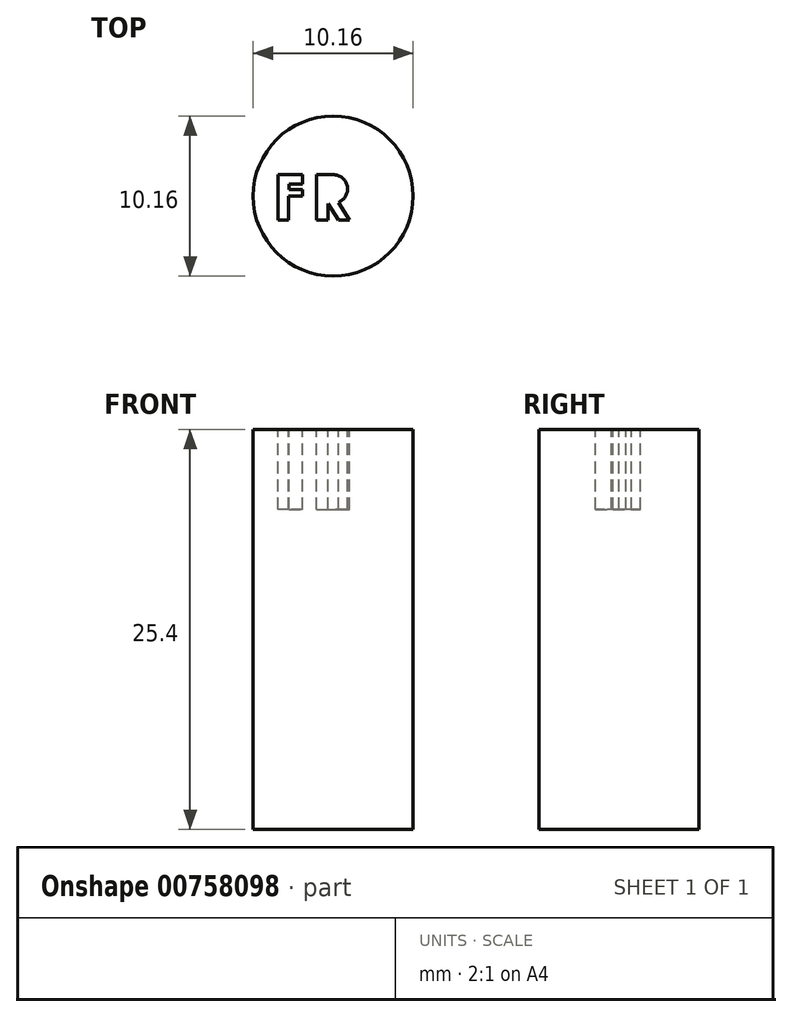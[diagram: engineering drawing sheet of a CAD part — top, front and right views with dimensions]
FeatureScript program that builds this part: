
annotation { "Feature Type Name" : "Feature", "Feature Type Description" : "" }
export const myFeature = defineFeature(function(context is Context, id is Id, definition is map)
    precondition{}
    {
        {
            var Q0;
            Q0=qCreatedBy(makeId("Top.planeOp"),FACE);
            var sketch = newSketch(context, id + "F0", { "sketchPlane" : qUnion([Q0])});
            skCircle(sketch, "E0", {"center": v(0, 0) * mm, "radius": 5.08 * mm});
            skSolve(sketch);
        }
        {
            var Q0;
            Q0=makeQuery(id+"F0.imprint","IMPRINT",FACE,{"disambiguationData":[TD([[makeQuery(id+"F0.imprint","IMPRINT",EDGE,{"derivedFrom":sQuery(id+"F0.wireOp",EDGE,"E0")}),1.0]])]});
            extrude(context, id + "F1", {"entities" : qUnion([Q0]), "depth" : 25.4 * mm, "offsetDistance" : 25.4 * mm});
        }
        {
            var Q0;
            Q0=makeQuery(id+"F1.opExtrude","CAP_FACE",FACE,{"disambiguationData":[OSD([sQuery(id+"F0.wireOp",EDGE,"E0")])],"isStart":false});
            var sketch = newSketch(context, id + "F2", { "sketchPlane" : qUnion([Q0])});
            skLineSegment(sketch, "E1", {"start": v(-3.5, -1.51) * mm, "end": v(-3.5, 1.36) * mm});
            skLineSegment(sketch, "E2", {"start": v(-1.93, 1.36) * mm, "end": v(-3.5, 1.36) * mm});
            skLineSegment(sketch, "E3", {"start": v(-1.93, 1.36) * mm, "end": v(-1.93, 0.78) * mm});
            skLineSegment(sketch, "E4", {"start": v(-1.93, 0.78) * mm, "end": v(-2.82, 0.78) * mm});
            skLineSegment(sketch, "E5", {"start": v(-2.82, 0.78) * mm, "end": v(-2.82, 0.43) * mm});
            skLineSegment(sketch, "E6", {"start": v(-2.82, 0.43) * mm, "end": v(-1.93, 0.43) * mm});
            skLineSegment(sketch, "E7", {"start": v(-1.93, 0.43) * mm, "end": v(-1.93, 0) * mm});
            skLineSegment(sketch, "E8", {"start": v(-1.93, 0) * mm, "end": v(-2.84, 0) * mm});
            skLineSegment(sketch, "E9", {"start": v(-2.84, 0) * mm, "end": v(-2.84, -1.51) * mm});
            skLineSegment(sketch, "E10", {"start": v(-2.84, -1.51) * mm, "end": v(-3.5, -1.51) * mm});
            skLineSegment(sketch, "E11", {"start": v(-1.04, 1.36) * mm, "end": v(-1.04, -1.51) * mm});
            skLineSegment(sketch, "E12", {"start": v(-1.04, -1.51) * mm, "end": v(-0.32, -1.51) * mm});
            skLineSegment(sketch, "E13", {"start": v(-0.32, -1.51) * mm, "end": v(-0.32, -0.48) * mm});
            skLineSegment(sketch, "E14", {"start": v(-0.32, -0.48) * mm, "end": v(0.34, -1.51) * mm});
            skLineSegment(sketch, "E15", {"start": v(0.34, -1.51) * mm, "end": v(1.04, -1.51) * mm});
            skLineSegment(sketch, "E16", {"start": v(1.04, -1.51) * mm, "end": v(0.33, -0.4) * mm});
            skLineSegment(sketch, "E17", {"start": v(-1.04, 1.36) * mm, "end": v(0, 1.36) * mm});
            skArc(sketch, "E18", {"start": v(0.33, -0.4) * mm, "mid": v(0.9, 0.62) * mm, "end": v(0, 1.36) * mm});
            skSolve(sketch);
        }
        {
            var Q0;
            Q0=makeQuery(id+"F2.imprint","IMPRINT",FACE,{"disambiguationData":[TD([[makeQuery(id+"F2.imprint","IMPRINT",EDGE,{"derivedFrom":sQuery(id+"F2.wireOp",EDGE,"E1")}),-1.0]])]});
            var Q1;
            Q1=makeQuery(id+"F2.imprint","IMPRINT",FACE,{"disambiguationData":[TD([[makeQuery(id+"F2.imprint","IMPRINT",EDGE,{"derivedFrom":sQuery(id+"F2.wireOp",EDGE,"E11")}),1.0]])]});
            extrude(context, id + "F3", {"entities" : qUnion([Q0, Q1]), "operationType" : NewBodyOperationType.REMOVE, "oppositeDirection" : true, "depth" : 5.08 * mm, "offsetDistance" : 25.4 * mm});
        }
    });
